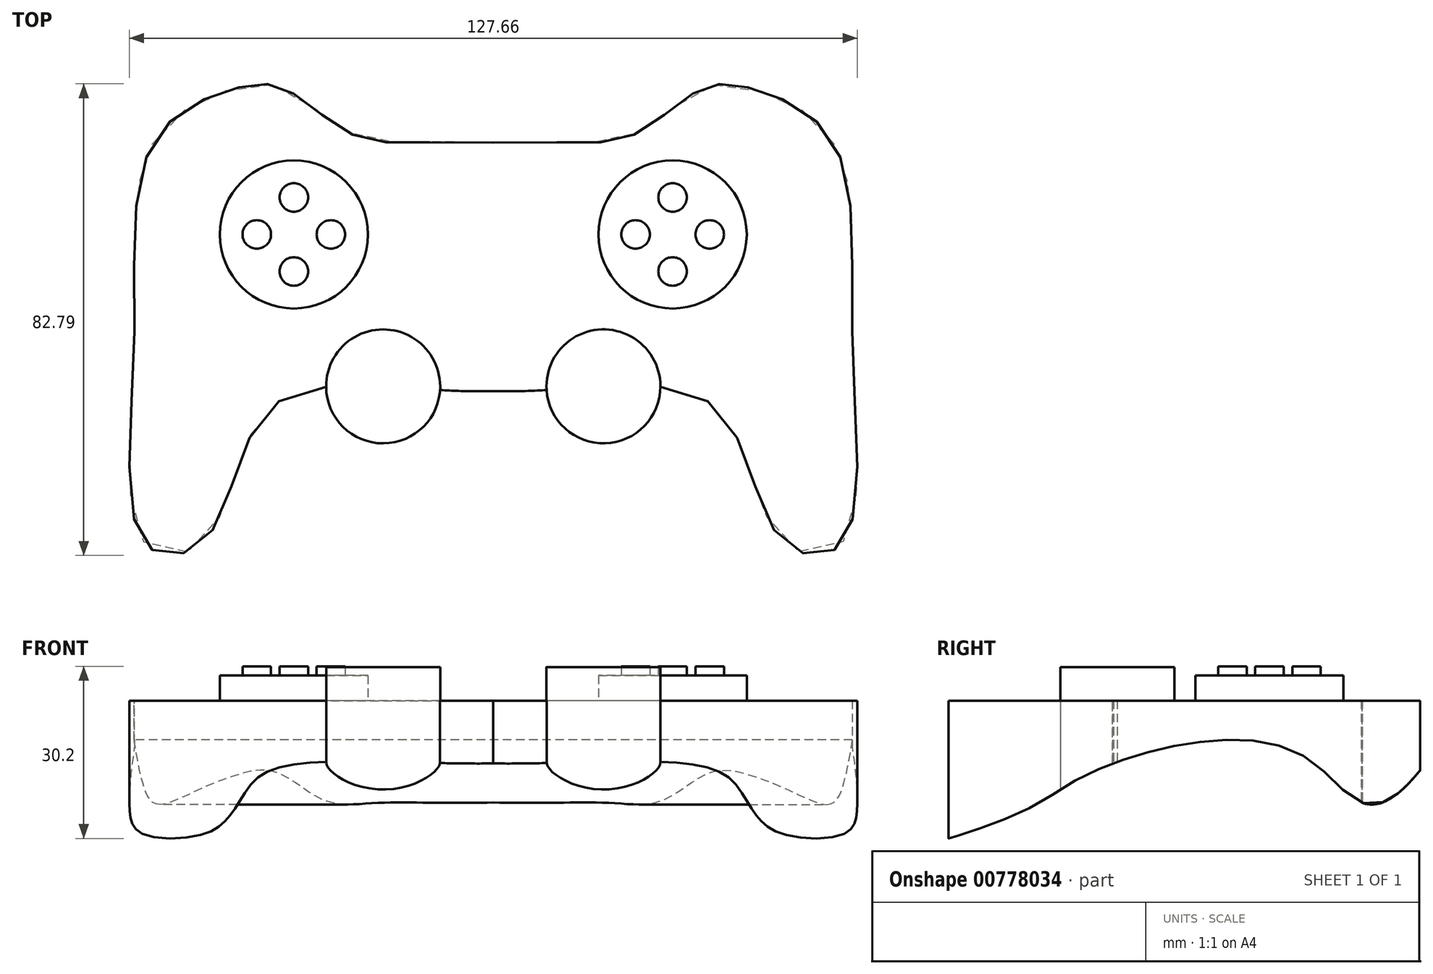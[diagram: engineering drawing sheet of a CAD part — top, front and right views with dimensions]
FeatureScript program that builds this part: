
annotation { "Feature Type Name" : "Feature", "Feature Type Description" : "" }
export const myFeature = defineFeature(function(context is Context, id is Id, definition is map)
    precondition{}
    {
        {
            var Q0;
            Q0=qCreatedBy(makeId("Top.planeOp"),FACE);
            var sketch = newSketch(context, id + "F0", { "sketchPlane" : qUnion([Q0])});
            skFitSpline(sketch, "E0.MirrorCS", {"points": [v(0, -8.08) * mm, v(38.65, -10.63) * mm, v(50.27, -33.86) * mm, v(60.75, -35.27) * mm, v(63.01, 0) * mm, v(59.33, 36.11) * mm, v(44.88, 45.18) * mm, v(36.38, 44.9) * mm, v(24.77, 36.96) * mm, v(0, 35.54) * mm], "startDerivative": vector(291.81, -11.44) * mm, "endDerivative": vector(-342.95, -14.6) * mm});
            skFitSpline(sketch, "E1.MirrorCS", {"points": [v(0, -8.08) * mm, v(-38.65, -10.63) * mm, v(-50.27, -33.86) * mm, v(-60.75, -35.27) * mm, v(-63.01, 0) * mm, v(-59.33, 36.11) * mm, v(-44.88, 45.18) * mm, v(-36.38, 44.9) * mm, v(-24.77, 36.96) * mm, v(0, 35.54) * mm], "startDerivative": vector(-291.81, -11.44) * mm, "endDerivative": vector(342.95, -14.6) * mm});
            skCircle(sketch, "E2", {"center": v(-19.33, -7.27) * mm, "radius": 10 * mm});
            skCircle(sketch, "E3", {"center": v(19.33, -7.27) * mm, "radius": 10 * mm});
            skCircle(sketch, "E4", {"center": v(-34.98, 19.4) * mm, "radius": 13 * mm});
            skCircle(sketch, "E5", {"center": v(31.46, 19.4) * mm, "radius": 13 * mm});
            skLineSegment(sketch, "E6", {"start": v(-34.98, 19.4) * mm, "end": v(-34.98, 32.4) * mm, "construction": true});
            skLineSegment(sketch, "E7", {"start": v(-34.98, 32.4) * mm, "end": v(-34.98, 25.9) * mm, "construction": true});
            skLineSegment(sketch, "E8", {"start": v(-34.98, 19.4) * mm, "end": v(-34.98, 6.4) * mm, "construction": true});
            skLineSegment(sketch, "E9", {"start": v(-34.98, 6.4) * mm, "end": v(-34.98, 12.9) * mm, "construction": true});
            skLineSegment(sketch, "E10", {"start": v(-34.98, 19.4) * mm, "end": v(-21.98, 19.4) * mm, "construction": true});
            skLineSegment(sketch, "E11", {"start": v(-21.98, 19.4) * mm, "end": v(-28.48, 19.4) * mm, "construction": true});
            skLineSegment(sketch, "E12", {"start": v(-34.98, 19.4) * mm, "end": v(-47.98, 19.4) * mm, "construction": true});
            skLineSegment(sketch, "E13", {"start": v(-47.98, 19.4) * mm, "end": v(-41.48, 19.4) * mm, "construction": true});
            skLineSegment(sketch, "E14", {"start": v(31.46, 19.4) * mm, "end": v(44.46, 19.4) * mm, "construction": true});
            skLineSegment(sketch, "E15", {"start": v(44.46, 19.4) * mm, "end": v(37.96, 19.4) * mm, "construction": true});
            skLineSegment(sketch, "E16", {"start": v(31.46, 19.4) * mm, "end": v(18.46, 19.4) * mm, "construction": true});
            skLineSegment(sketch, "E17", {"start": v(18.46, 19.4) * mm, "end": v(24.96, 19.4) * mm, "construction": true});
            skLineSegment(sketch, "E18", {"start": v(31.46, 19.4) * mm, "end": v(31.46, 32.4) * mm, "construction": true});
            skLineSegment(sketch, "E19", {"start": v(31.46, 32.4) * mm, "end": v(31.46, 25.9) * mm, "construction": true});
            skLineSegment(sketch, "E20", {"start": v(31.46, 19.4) * mm, "end": v(31.46, 6.4) * mm, "construction": true});
            skLineSegment(sketch, "E21", {"start": v(31.46, 6.4) * mm, "end": v(31.46, 12.9) * mm, "construction": true});
            skCircle(sketch, "E22", {"center": v(-34.98, 25.9) * mm, "radius": 2.5 * mm});
            skCircle(sketch, "E23", {"center": v(-28.48, 19.4) * mm, "radius": 2.5 * mm});
            skCircle(sketch, "E24", {"center": v(-34.98, 12.9) * mm, "radius": 2.5 * mm});
            skCircle(sketch, "E25", {"center": v(-41.48, 19.4) * mm, "radius": 2.5 * mm});
            skCircle(sketch, "E26", {"center": v(31.46, 25.9) * mm, "radius": 2.5 * mm});
            skCircle(sketch, "E27", {"center": v(37.96, 19.4) * mm, "radius": 2.5 * mm});
            skCircle(sketch, "E28", {"center": v(31.46, 12.9) * mm, "radius": 2.5 * mm});
            skCircle(sketch, "E29", {"center": v(24.96, 19.4) * mm, "radius": 2.5 * mm});
            skSolve(sketch);
        }
        {
            var Q0;
            Q0=qCreatedBy(makeId("Right.planeOp"),FACE);
            var sketch = newSketch(context, id + "F1", { "sketchPlane" : qUnion([Q0])});
            skFitSpline(sketch, "E30", {"points": [v(-37.5, 0.63) * mm, v(-12.04, 12.32) * mm, v(25.64, 15.16) * mm, v(46.82, 14.02) * mm], "startDerivative": vector(160.44, 47.03) * mm, "endDerivative": vector(115.25, 151.97) * mm});
            skLineSegment(sketch, "E31", {"start": v(46.82, 14.02) * mm, "end": v(46.82, -1.45) * mm});
            skLineSegment(sketch, "E32", {"start": v(46.82, -1.45) * mm, "end": v(-36.97, -1.45) * mm});
            skLineSegment(sketch, "E33", {"start": v(-36.97, -1.45) * mm, "end": v(-37.5, 0.63) * mm});
            skSolve(sketch);
        }
        {
            var Q0;
            Q0=makeQuery(id+"F0.imprint","IMPRINT",FACE,{"disambiguationData":[TD([[makeQuery(id+"F0.imprint","IMPRINT",EDGE,{"derivedFrom":sQuery(id+"F0.wireOp",EDGE,"E4")}),-1.0]])]});
            extrude(context, id + "F2", {"entities" : qUnion([Q0]), "depth" : 25 * mm, "offsetDistance" : 25 * mm});
        }
        {
            var Q0;
            {var subQ0=sQuery(id+"F0.wireOp",EDGE,"E3");var subQ1=sQuery(id+"F0.wireOp",EDGE,"E0.MirrorCS");var subQ2=makeQuery(id+"F0.imprint","INTERSECT",VERTEX,{"disambiguationData":[OD(0.0)],"derivedFrom":[subQ1,subQ0]});Q0=makeQuery(id+"F0.imprint","IMPRINT",FACE,{"disambiguationData":[TD([[makeQuery(id+"F0.imprint","IMPRINT",EDGE,{"disambiguationData":[TD([[subQ2,-1.0]])],"derivedFrom":subQ1}),-1.0]])]});}
            var Q1;
            {var subQ0=sQuery(id+"F0.wireOp",EDGE,"E3");var subQ1=sQuery(id+"F0.wireOp",EDGE,"E0.MirrorCS");var subQ2=makeQuery(id+"F0.imprint","INTERSECT",VERTEX,{"disambiguationData":[OD(0.0)],"derivedFrom":[subQ1,subQ0]});Q1=makeQuery(id+"F0.imprint","IMPRINT",FACE,{"disambiguationData":[TD([[makeQuery(id+"F0.imprint","IMPRINT",EDGE,{"disambiguationData":[TD([[subQ2,-1.0]])],"derivedFrom":subQ1}),1.0]])]});}
            var Q2;
            {var subQ0=sQuery(id+"F0.wireOp",EDGE,"E2");var subQ1=sQuery(id+"F0.wireOp",EDGE,"E1.MirrorCS");var subQ2=makeQuery(id+"F0.imprint","INTERSECT",VERTEX,{"disambiguationData":[OD(0.0)],"derivedFrom":[subQ1,subQ0]});Q2=makeQuery(id+"F0.imprint","IMPRINT",FACE,{"disambiguationData":[TD([[makeQuery(id+"F0.imprint","IMPRINT",EDGE,{"disambiguationData":[TD([[subQ2,-1.0]])],"derivedFrom":subQ1}),-1.0]])]});}
            var Q3;
            {var subQ0=sQuery(id+"F0.wireOp",EDGE,"E2");var subQ1=sQuery(id+"F0.wireOp",EDGE,"E1.MirrorCS");var subQ2=makeQuery(id+"F0.imprint","INTERSECT",VERTEX,{"disambiguationData":[OD(0.0)],"derivedFrom":[subQ1,subQ0]});Q3=makeQuery(id+"F0.imprint","IMPRINT",FACE,{"disambiguationData":[TD([[makeQuery(id+"F0.imprint","IMPRINT",EDGE,{"disambiguationData":[TD([[subQ2,-1.0]])],"derivedFrom":subQ1}),1.0]])]});}
            extrude(context, id + "F3", {"entities" : qUnion([Q0, Q1, Q2, Q3]), "operationType" : NewBodyOperationType.ADD, "depth" : 30.9 * mm, "offsetDistance" : 25 * mm});
        }
        {
            var Q0;
            Q0=makeQuery(id+"F0.imprint","IMPRINT",FACE,{"disambiguationData":[TD([[makeQuery(id+"F0.imprint","IMPRINT",EDGE,{"derivedFrom":sQuery(id+"F0.wireOp",EDGE,"E5")}),1.0]])]});
            var Q1;
            Q1=makeQuery(id+"F0.imprint","IMPRINT",FACE,{"disambiguationData":[TD([[makeQuery(id+"F0.imprint","IMPRINT",EDGE,{"derivedFrom":sQuery(id+"F0.wireOp",EDGE,"E4")}),1.0]])]});
            extrude(context, id + "F4", {"entities" : qUnion([Q0, Q1]), "operationType" : NewBodyOperationType.ADD, "depth" : 29.4 * mm, "offsetDistance" : 25 * mm});
        }
        {
            var Q0;
            Q0=makeQuery(id+"F0.imprint","IMPRINT",FACE,{"disambiguationData":[TD([[makeQuery(id+"F0.imprint","IMPRINT",EDGE,{"derivedFrom":sQuery(id+"F0.wireOp",EDGE,"E26")}),1.0]])]});
            var Q1;
            Q1=makeQuery(id+"F0.imprint","IMPRINT",FACE,{"disambiguationData":[TD([[makeQuery(id+"F0.imprint","IMPRINT",EDGE,{"derivedFrom":sQuery(id+"F0.wireOp",EDGE,"E27")}),1.0]])]});
            var Q2;
            Q2=makeQuery(id+"F0.imprint","IMPRINT",FACE,{"disambiguationData":[TD([[makeQuery(id+"F0.imprint","IMPRINT",EDGE,{"derivedFrom":sQuery(id+"F0.wireOp",EDGE,"E28")}),1.0]])]});
            var Q3;
            Q3=makeQuery(id+"F0.imprint","IMPRINT",FACE,{"disambiguationData":[TD([[makeQuery(id+"F0.imprint","IMPRINT",EDGE,{"derivedFrom":sQuery(id+"F0.wireOp",EDGE,"E29")}),1.0]])]});
            var Q4;
            Q4=makeQuery(id+"F0.imprint","IMPRINT",FACE,{"disambiguationData":[TD([[makeQuery(id+"F0.imprint","IMPRINT",EDGE,{"derivedFrom":sQuery(id+"F0.wireOp",EDGE,"E22")}),1.0]])]});
            var Q5;
            Q5=makeQuery(id+"F0.imprint","IMPRINT",FACE,{"disambiguationData":[TD([[makeQuery(id+"F0.imprint","IMPRINT",EDGE,{"derivedFrom":sQuery(id+"F0.wireOp",EDGE,"E23")}),1.0]])]});
            var Q6;
            Q6=makeQuery(id+"F0.imprint","IMPRINT",FACE,{"disambiguationData":[TD([[makeQuery(id+"F0.imprint","IMPRINT",EDGE,{"derivedFrom":sQuery(id+"F0.wireOp",EDGE,"E25")}),1.0]])]});
            var Q7;
            Q7=makeQuery(id+"F0.imprint","IMPRINT",FACE,{"disambiguationData":[TD([[makeQuery(id+"F0.imprint","IMPRINT",EDGE,{"derivedFrom":sQuery(id+"F0.wireOp",EDGE,"E24")}),1.0]])]});
            extrude(context, id + "F5", {"entities" : qUnion([Q0, Q1, Q2, Q3, Q4, Q5, Q6, Q7]), "operationType" : NewBodyOperationType.ADD, "depth" : 31 * mm, "offsetDistance" : 25 * mm});
        }
        {
            var Q0;
            Q0 = qSketchRegion(id + "F1", true);
            extrude(context, id + "F6", {"entities" : qUnion([Q0]), "operationType" : NewBodyOperationType.REMOVE, "endBound" : BoundingType.SYMMETRIC, "oppositeDirection" : true, "depth" : 150 * mm, "offsetDistance" : 25 * mm});
        }
    });
